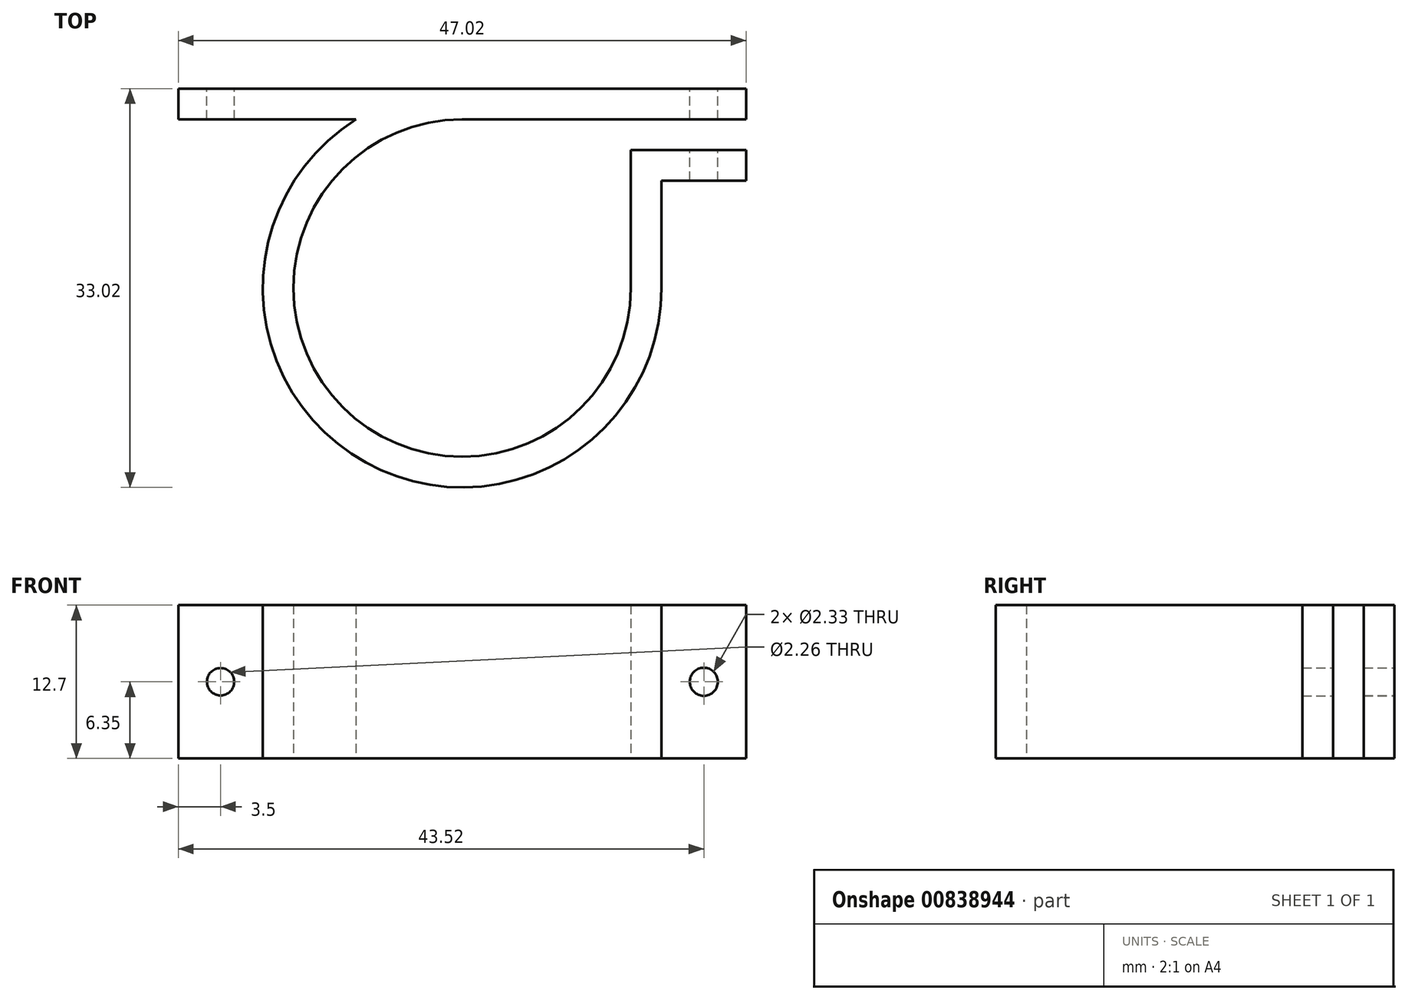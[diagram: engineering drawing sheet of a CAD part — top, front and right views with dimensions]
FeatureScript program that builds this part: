
annotation { "Feature Type Name" : "Feature", "Feature Type Description" : "" }
export const myFeature = defineFeature(function(context is Context, id is Id, definition is map)
    precondition{}
    {
        {
            var Q0;
            Q0=qCreatedBy(makeId("Top.planeOp"),FACE);
            var sketch = newSketch(context, id + "F0", { "sketchPlane" : qUnion([Q0])});
            skArc(sketch, "E0", {"start": v(0, 13.97) * mm, "mid": v(-9.88, -9.88) * mm, "end": v(13.97, 0) * mm});
            skArc(sketch, "E1", {"start": v(16.51, 0) * mm, "mid": v(-7.98, -14.45) * mm, "end": v(-8.8, 13.97) * mm});
            skLineSegment(sketch, "E2", {"start": v(-8.8, 13.97) * mm, "end": v(-23.51, 13.97) * mm});
            skLineSegment(sketch, "E3", {"start": v(-23.51, 13.97) * mm, "end": v(-23.51, 16.51) * mm});
            skLineSegment(sketch, "E4", {"start": v(-23.51, 16.51) * mm, "end": v(23.51, 16.51) * mm});
            skLineSegment(sketch, "E5", {"start": v(23.51, 16.51) * mm, "end": v(23.51, 13.97) * mm});
            skLineSegment(sketch, "E6", {"start": v(0, 13.97) * mm, "end": v(23.51, 13.97) * mm});
            skLineSegment(sketch, "E7", {"start": v(13.97, 0) * mm, "end": v(13.97, 11.43) * mm});
            skLineSegment(sketch, "E8", {"start": v(13.97, 11.43) * mm, "end": v(23.5, 11.43) * mm});
            skLineSegment(sketch, "E9", {"start": v(23.5, 11.43) * mm, "end": v(23.5, 8.9) * mm});
            skLineSegment(sketch, "E10", {"start": v(16.51, 0) * mm, "end": v(16.51, 8.9) * mm});
            skLineSegment(sketch, "E11", {"start": v(16.51, 8.9) * mm, "end": v(23.5, 8.9) * mm});
            skSolve(sketch);
        }
        {
            var Q0;
            Q0 = qSketchRegion(id + "F0", true);
            extrude(context, id + "F1", {"entities" : qUnion([Q0]), "depth" : 12.7 * mm, "offsetDistance" : 25.4 * mm});
        }
        {
            var Q0;
            Q0=makeQuery(id+"F1.opExtrude","SWEPT_FACE",FACE,{"disambiguationData":[OSD([sQuery(id+"F0.wireOp",EDGE,"E4")])]});
            var sketch = newSketch(context, id + "F2", { "sketchPlane" : qUnion([Q0])});
            skCircle(sketch, "E12", {"center": v(20.01, 6.35) * mm, "radius": 1.13 * mm});
            skCircle(sketch, "E13", {"center": v(-20.01, 6.35) * mm, "radius": 1.16 * mm});
            skSolve(sketch);
        }
        {
            var Q0;
            Q0 = qSketchRegion(id + "F2", true);
            extrude(context, id + "F3", {"entities" : qUnion([Q0]), "operationType" : NewBodyOperationType.REMOVE, "endBound" : BoundingType.THROUGH_ALL, "oppositeDirection" : true, "depth" : 25.4 * mm, "offsetDistance" : 25.4 * mm});
        }
    });
